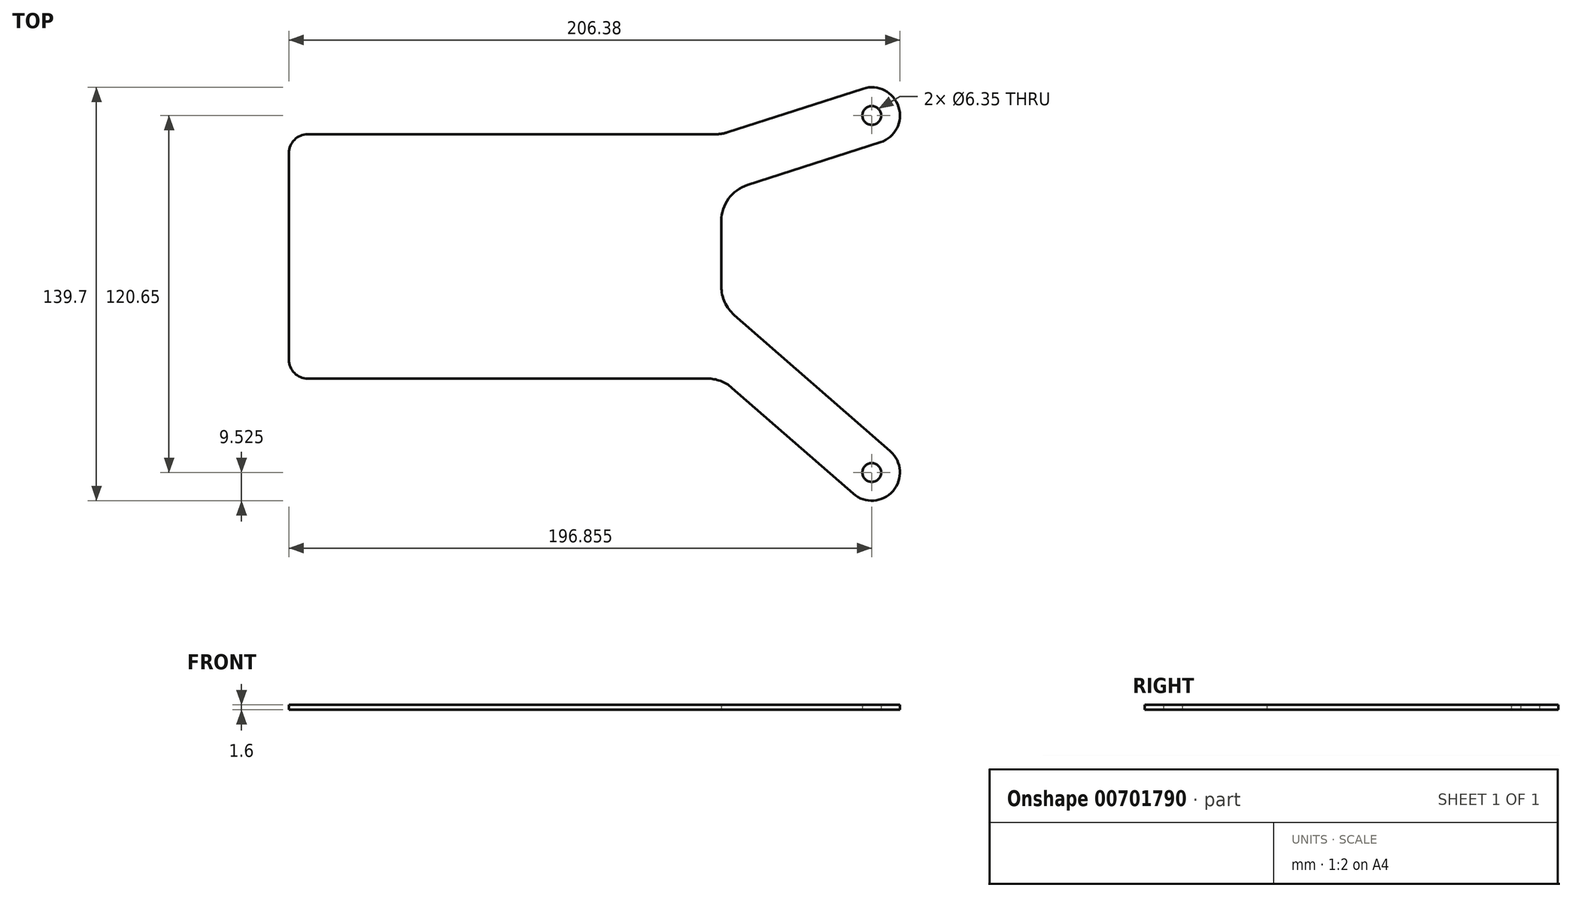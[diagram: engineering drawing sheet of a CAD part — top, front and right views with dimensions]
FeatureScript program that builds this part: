
annotation { "Feature Type Name" : "Feature", "Feature Type Description" : "" }
export const myFeature = defineFeature(function(context is Context, id is Id, definition is map)
    precondition{}
    {
        {
            var Q0;
            Q0=qCreatedBy(makeId("Top.planeOp"),FACE);
            var sketch = newSketch(context, id + "F0", { "sketchPlane" : qUnion([Q0])});
            skLineSegment(sketch, "E0.bottom", {"start": v(-66.68, 41.28) * mm, "end": v(71.03, 41.28) * mm});
            skLineSegment(sketch, "E0.top", {"start": v(-66.68, -41.27) * mm, "end": v(68.26, -41.27) * mm});
            skLineSegment(sketch, "E0.left", {"start": v(-73.03, 34.93) * mm, "end": v(-73.03, -34.92) * mm});
            skLineSegment(sketch, "E0.right", {"start": v(73.03, 12) * mm, "end": v(73.03, -10.2) * mm});
            skPoint(sketch, "E0.middle", {"position": v(0, 0) * mm});
            skCircle(sketch, "E1", {"center": v(123.83, 47.62) * mm, "radius": 3.18 * mm});
            skCircle(sketch, "E2", {"center": v(123.83, 47.62) * mm, "radius": 9.53 * mm});
            skLineSegment(sketch, "E3", {"start": v(74.92, 41.89) * mm, "end": v(120.9, 56.7) * mm});
            skLineSegment(sketch, "E4", {"start": v(81.83, 24.1) * mm, "end": v(126.74, 38.56) * mm});
            skCircle(sketch, "E5", {"center": v(123.83, -73.03) * mm, "radius": 3.18 * mm});
            skCircle(sketch, "E6", {"center": v(123.83, -73.03) * mm, "radius": 9.53 * mm});
            skLineSegment(sketch, "E7", {"start": v(76.61, -44.41) * mm, "end": v(117.56, -80.2) * mm});
            skLineSegment(sketch, "E8", {"start": v(130.1, -65.85) * mm, "end": v(77.37, -19.77) * mm});
            skArc(sketch, "E9.filletArc", {"start": v(81.83, 24.1) * mm, "mid": v(75.46, 19.49) * mm, "end": v(73.03, 12) * mm});
            skArc(sketch, "E10.filletArc", {"start": v(73.03, -10.2) * mm, "mid": v(74.16, -15.46) * mm, "end": v(77.37, -19.77) * mm});
            skPoint(sketch, "E11.visualSharp", {"position": v(-73.03, 41.27) * mm});
            skArc(sketch, "E11.filletArc", {"start": v(-66.68, 41.28) * mm, "mid": v(-71.17, 39.42) * mm, "end": v(-73.03, 34.93) * mm});
            skPoint(sketch, "E12.visualSharp", {"position": v(-73.03, -41.28) * mm});
            skArc(sketch, "E12.filletArc", {"start": v(-73.03, -34.92) * mm, "mid": v(-71.17, -39.42) * mm, "end": v(-66.68, -41.27) * mm});
            skPoint(sketch, "E13.visualSharp", {"position": v(73.03, 41.28) * mm});
            skArc(sketch, "E13.filletArc", {"start": v(71.03, 41.27) * mm, "mid": v(73, 41.43) * mm, "end": v(74.92, 41.89) * mm});
            skPoint(sketch, "E14.visualSharp", {"position": v(73.03, -41.27) * mm});
            skArc(sketch, "E14.filletArc", {"start": v(76.61, -44.41) * mm, "mid": v(72.72, -42.09) * mm, "end": v(68.26, -41.27) * mm});
            skSolve(sketch);
        }
        {
            var Q0;
            Q0=makeQuery(id+"F0.imprint","IMPRINT",FACE,{"disambiguationData":[TD([[makeQuery(id+"F0.imprint","IMPRINT",EDGE,{"derivedFrom":sQuery(id+"F0.wireOp",EDGE,"E0.bottom")}),-1.0]])]});
            var Q1;
            Q1=makeQuery(id+"F0.imprint","IMPRINT",FACE,{"disambiguationData":[TD([[makeQuery(id+"F0.imprint","IMPRINT",EDGE,{"derivedFrom":sQuery(id+"F0.wireOp",EDGE,"E1")}),-1.0]])]});
            var Q2;
            Q2=makeQuery(id+"F0.imprint","IMPRINT",FACE,{"disambiguationData":[TD([[makeQuery(id+"F0.imprint","IMPRINT",EDGE,{"derivedFrom":sQuery(id+"F0.wireOp",EDGE,"E5")}),-1.0]])]});
            extrude(context, id + "F1", {"entities" : qUnion([Q0, Q1, Q2]), "depth" : 1.6 * mm, "offsetDistance" : 25.4 * mm});
        }
    });
